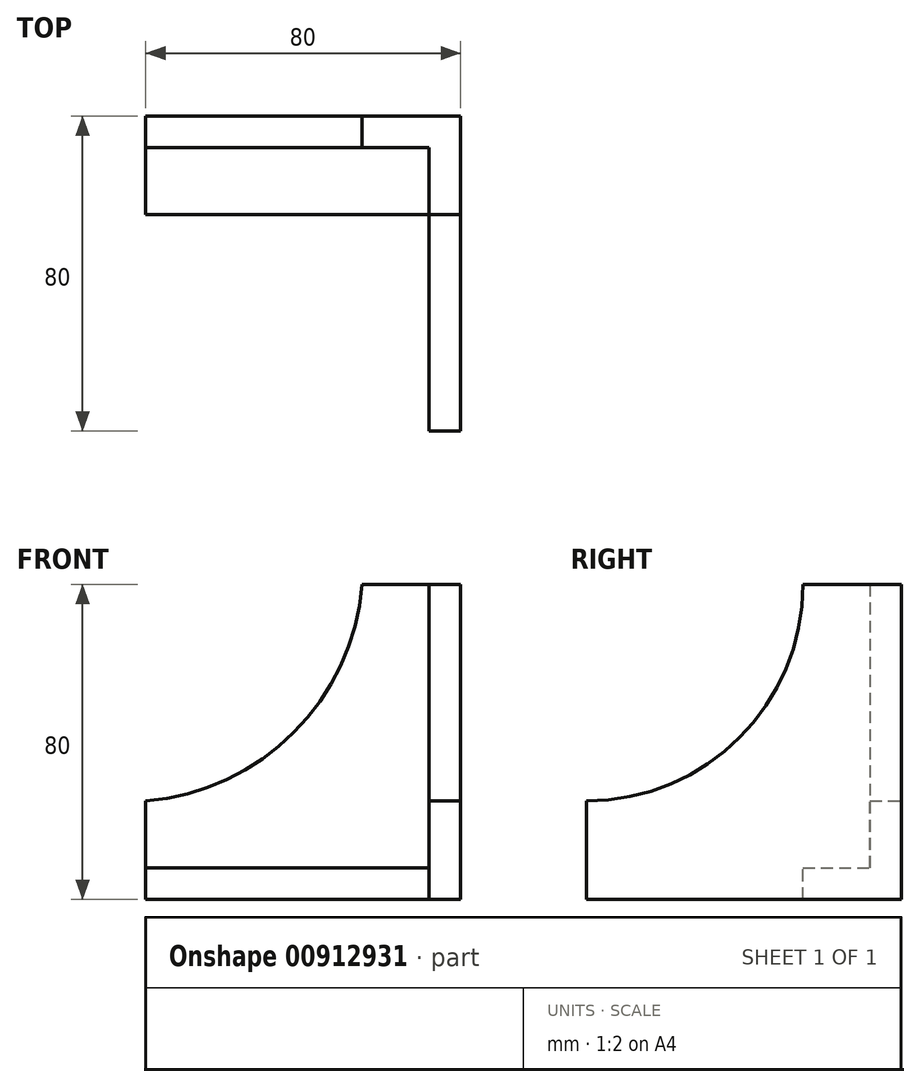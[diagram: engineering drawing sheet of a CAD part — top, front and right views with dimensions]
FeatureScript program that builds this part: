
annotation { "Feature Type Name" : "Feature", "Feature Type Description" : "" }
export const myFeature = defineFeature(function(context is Context, id is Id, definition is map)
    precondition{}
    {
        {
            var Q0;
            Q0=qCreatedBy(makeId("Front.planeOp"),FACE);
            var sketch = newSketch(context, id + "F0", { "sketchPlane" : qUnion([Q0])});
            skLineSegment(sketch, "E0.bottom", {"start": v(40, -4) * mm, "end": v(-40, -4) * mm});
            skPoint(sketch, "E0.middle", {"position": v(0, 0) * mm});
            skLineSegment(sketch, "E1", {"start": v(40, 76) * mm, "end": v(15, 76) * mm});
            skLineSegment(sketch, "E2", {"start": v(-40, -4) * mm, "end": v(-40, 21) * mm});
            skArc(sketch, "E3", {"start": v(-40, 21) * mm, "mid": v(-2.38, 38.38) * mm, "end": v(15, 76) * mm});
            skLineSegment(sketch, "E4", {"start": v(40, 76) * mm, "end": v(32, 76) * mm});
            skLineSegment(sketch, "E5", {"start": v(32, 76) * mm, "end": v(32, 4) * mm});
            skLineSegment(sketch, "E6", {"start": v(-40, 4) * mm, "end": v(32, 4) * mm});
            skLineSegment(sketch, "E7", {"start": v(40, -4) * mm, "end": v(40, 76) * mm});
            skSolve(sketch);
        }
        {
            var Q0;
            {var subQ2=sQuery(id+"F0.wireOp",EDGE,"E0.bottom");Q0=makeQuery(id+"F0.imprint","IMPRINT",FACE,{"disambiguationData":[TD([[makeQuery(id+"F0.imprint","IMPRINT",EDGE,{"derivedFrom":subQ2}),-1.0]])]});}
            extrude(context, id + "F1", {"entities" : qUnion([Q0]), "depth" : 25 * mm, "offsetDistance" : 25 * mm});
        }
        {
            var Q0;
            Q0=makeQuery(id+"F1.opExtrude","CAP_FACE",FACE,{"disambiguationData":[OSD([sQuery(id+"F0.wireOp",EDGE,"E0.bottom"),sQuery(id+"F0.wireOp",EDGE,"E1"),sQuery(id+"F0.wireOp",EDGE,"E2"),sQuery(id+"F0.wireOp",EDGE,"E5"),sQuery(id+"F0.wireOp",EDGE,"E6"),sQuery(id+"F0.wireOp",EDGE,"E7")])],"isStart":true});
            var sketch = newSketch(context, id + "F2", { "sketchPlane" : qUnion([Q0])});
            skLineSegment(sketch, "E8", {"start": v(40, -4) * mm, "end": v(40, 21) * mm});
            skLineSegment(sketch, "E9", {"start": v(-40, 76) * mm, "end": v(-15, 76) * mm});
            skArc(sketch, "E10", {"start": v(-15, 76) * mm, "mid": v(2.38, 38.38) * mm, "end": v(40, 21) * mm});
            skSolve(sketch);
        }
        {
            var Q0;
            {var subQ0=sQuery(id+"F2.wireOp",EDGE,"E10");Q0=makeQuery(id+"F2.imprint","IMPRINT",FACE,{"disambiguationData":[TD([[makeQuery(id+"F2.imprint","IMPRINT",EDGE,{"derivedFrom":subQ0}),-1.0]])]});}
            extrude(context, id + "F3", {"entities" : qUnion([Q0]), "operationType" : NewBodyOperationType.ADD, "depth" : -8 * mm, "offsetDistance" : 25 * mm});
        }
        {
            var Q0;
            Q0=makeQuery(id+"F1.opExtrude","SWEPT_FACE",FACE,{"disambiguationData":[OSD([sQuery(id+"F0.wireOp",EDGE,"E7")])]});
            var sketch = newSketch(context, id + "F4", { "sketchPlane" : qUnion([Q0])});
            skLineSegment(sketch, "E11", {"start": v(0, -4) * mm, "end": v(-80, -4) * mm});
            skLineSegment(sketch, "E12", {"start": v(-80, -4) * mm, "end": v(-80, 21) * mm});
            skArc(sketch, "E13", {"start": v(-80, 21) * mm, "mid": v(-41.1, 37.1) * mm, "end": v(-25, 76) * mm});
            skSolve(sketch);
        }
        {
            var Q0;
            {var subQ2=sQuery(id+"F4.wireOp",EDGE,"E12");Q0=makeQuery(id+"F4.imprint","IMPRINT",FACE,{"disambiguationData":[TD([[makeQuery(id+"F4.imprint","IMPRINT",EDGE,{"derivedFrom":subQ2}),-1.0]])]});}
            extrude(context, id + "F5", {"entities" : qUnion([Q0]), "operationType" : NewBodyOperationType.ADD, "depth" : -8 * mm, "offsetDistance" : 25 * mm});
        }
    });
